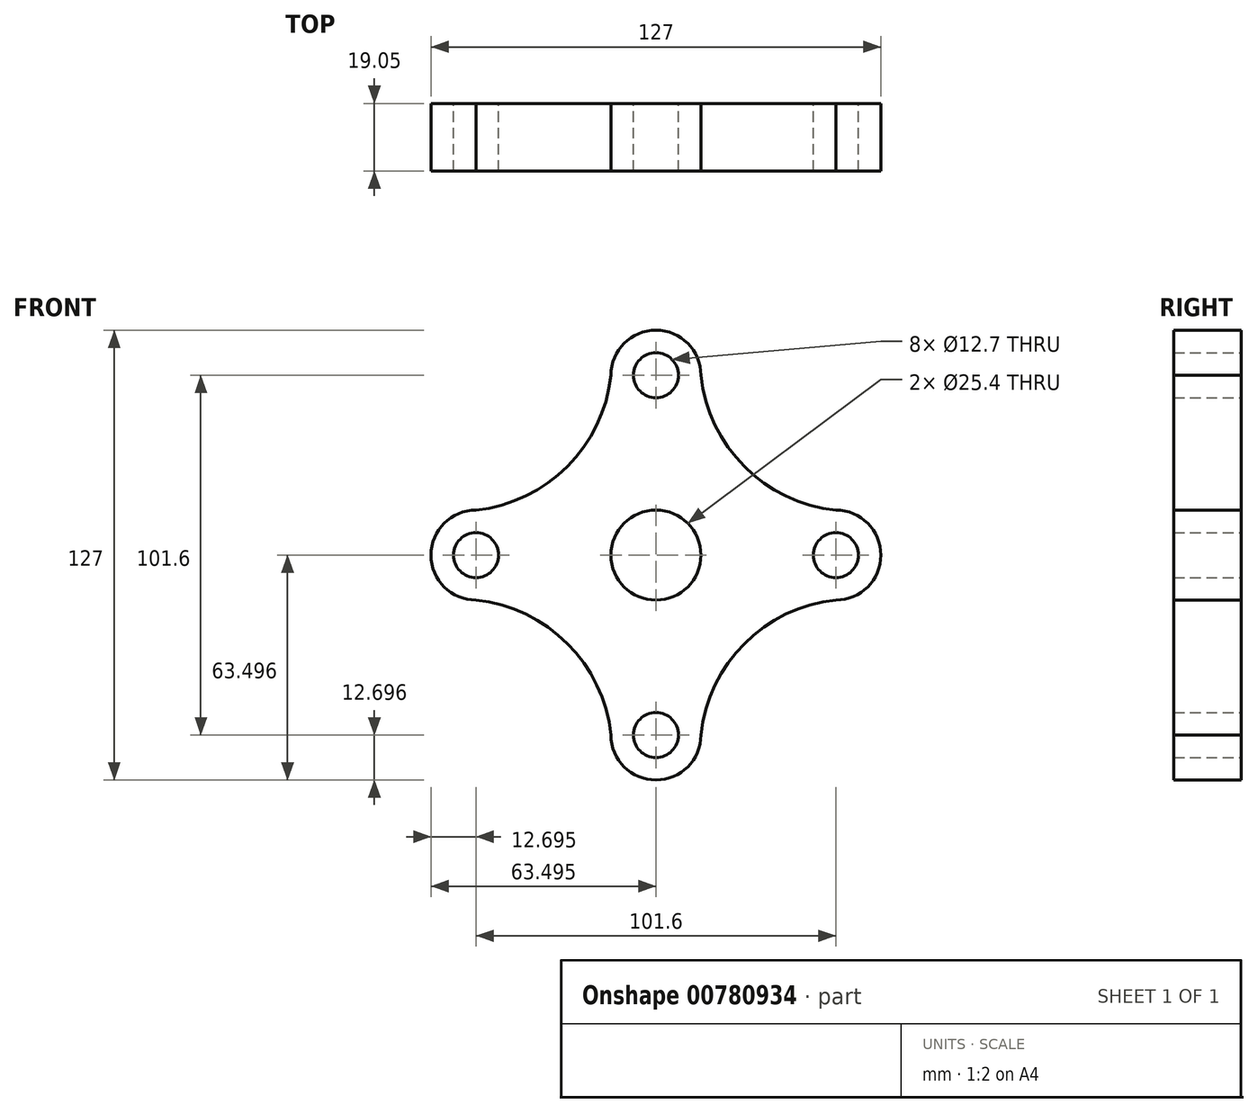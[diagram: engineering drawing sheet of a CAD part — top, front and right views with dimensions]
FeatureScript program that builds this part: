
annotation { "Feature Type Name" : "Feature", "Feature Type Description" : "" }
export const myFeature = defineFeature(function(context is Context, id is Id, definition is map)
    precondition{}
    {
        {
            var Q0;
            Q0=qCreatedBy(makeId("Front.planeOp"),FACE);
            var sketch = newSketch(context, id + "F0", { "sketchPlane" : qUnion([Q0])});
            skCircle(sketch, "E0", {"center": v(-51.08, 0.48) * mm, "radius": 6.35 * mm});
            skCircle(sketch, "E1", {"center": v(50.52, 0.48) * mm, "radius": 6.35 * mm});
            skCircle(sketch, "E2", {"center": v(-0.28, 0.48) * mm, "radius": 12.7 * mm});
            skCircle(sketch, "E3", {"center": v(-0.28, -50.32) * mm, "radius": 6.35 * mm});
            skCircle(sketch, "E4", {"center": v(-0.28, 51.28) * mm, "radius": 6.35 * mm});
            skArc(sketch, "E5", {"start": v(-51.08, 13.18) * mm, "mid": v(-25.31, 25.5) * mm, "end": v(-12.98, 51.28) * mm});
            skArc(sketch, "E6", {"start": v(12.42, 51.28) * mm, "mid": v(-0.28, 63.98) * mm, "end": v(-12.98, 51.28) * mm});
            skArc(sketch, "E7", {"start": v(-51.08, 13.18) * mm, "mid": v(-63.78, 0.48) * mm, "end": v(-51.08, -12.22) * mm});
            skPoint(sketch, "E8.trimOffspring.end.orphan", {"position": v(-51.08, 51.28) * mm});
            skArc(sketch, "E9", {"start": v(12.42, 51.28) * mm, "mid": v(24.7, 25.46) * mm, "end": v(50.52, 13.18) * mm});
            skArc(sketch, "E10", {"start": v(50.52, -12.22) * mm, "mid": v(63.22, 0.48) * mm, "end": v(50.52, 13.18) * mm});
            skPoint(sketch, "E11.orphan", {"position": v(50.52, 51.28) * mm});
            skArc(sketch, "E12", {"start": v(50.52, -12.22) * mm, "mid": v(24.7, -24.5) * mm, "end": v(12.42, -50.32) * mm});
            skArc(sketch, "E13", {"start": v(-12.98, -50.32) * mm, "mid": v(-0.28, -63.02) * mm, "end": v(12.42, -50.32) * mm});
            skArc(sketch, "E14", {"start": v(-12.98, -50.32) * mm, "mid": v(-25.27, -24.5) * mm, "end": v(-51.08, -12.22) * mm});
            skPoint(sketch, "E15.orphan", {"position": v(-51.08, -50.32) * mm});
            skPoint(sketch, "E16.orphan", {"position": v(50.52, -50.32) * mm});
            skSolve(sketch);
        }
        {
            var Q0;
            Q0=qSketchRegion(id+"F0",true);
            extrude(context, id + "F1", {"entities" : qUnion([Q0]), "depth" : 19.05 * mm, "offsetDistance" : 25.4 * mm});
        }
    });
